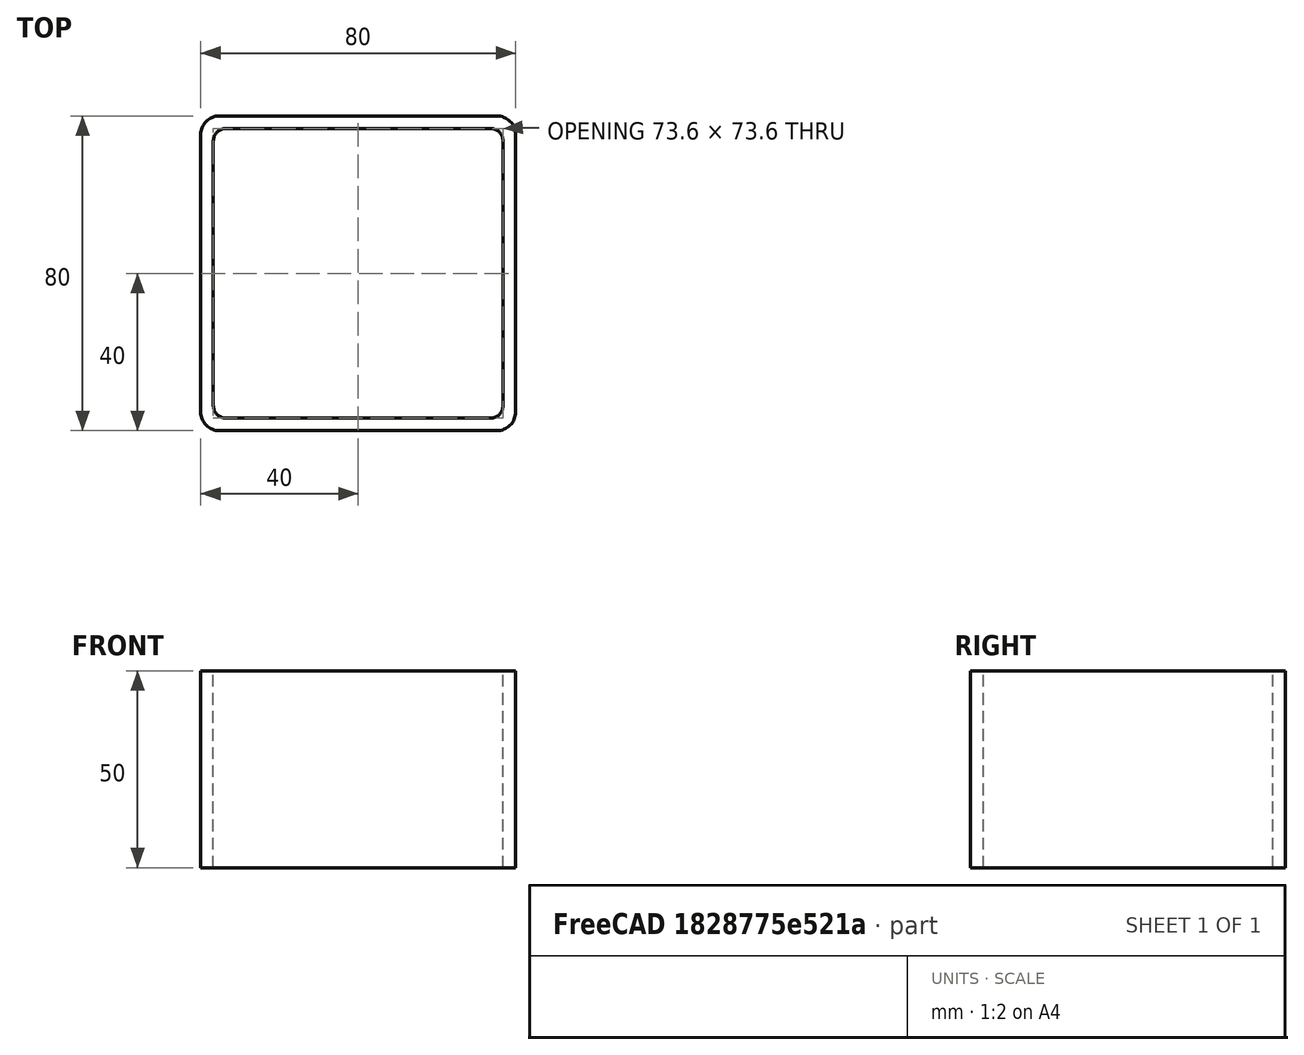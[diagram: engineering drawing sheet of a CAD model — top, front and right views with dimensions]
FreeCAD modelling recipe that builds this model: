
FCSTD DOCUMENT  (FreeCAD 0.15R4671 (Git))
Label: Square hollow section 80x80x3.2 EN10219 S235JRH
License: All rights reserved
LicenseURL: http://en.wikipedia.org/wiki/All_rights_reserved
objects: Sketcher::SketchObject×1, Part::Extrusion×1
note: 2 computed .brp shape members not serialized (recipe doc carries the construction recipe); baked Part::Feature solids carry a one-line shape summary decoded from their .brp

FEATURE [Sketcher::SketchObject] Sketch
  sketch-geometry (16):
    g0: LineSegment StartX=-33.6 StartY=36.8 StartZ=0 EndX=33.6 EndY=36.8 EndZ=0
    g1: LineSegment StartX=36.8 StartY=33.6 StartZ=0 EndX=36.8 EndY=-33.6 EndZ=0
    g2: LineSegment StartX=33.6 StartY=-36.8 StartZ=0 EndX=-33.6 EndY=-36.8 EndZ=0
    g3: LineSegment StartX=-36.8 StartY=-33.6 StartZ=0 EndX=-36.8 EndY=33.6 EndZ=0
    g4: LineSegment StartX=-35.2 StartY=40 StartZ=0 EndX=35.2 EndY=40 EndZ=0
    g5: LineSegment StartX=40 StartY=35.2 StartZ=0 EndX=40 EndY=-35.2 EndZ=0
    g6: LineSegment StartX=35.2 StartY=-40 StartZ=0 EndX=-35.2 EndY=-40 EndZ=0
    g7: LineSegment StartX=-40 StartY=-35.2 StartZ=0 EndX=-40 EndY=35.2 EndZ=0
    g8: ArcOfCircle CenterX=-33.6 CenterY=33.6 CenterZ=0 NormalX=0 NormalY=0 NormalZ=1 Radius=3.2 StartAngle=1.5708 EndAngle=3.14159
    g9: ArcOfCircle CenterX=33.6 CenterY=33.6 CenterZ=0 NormalX=0 NormalY=0 NormalZ=1 Radius=3.2 StartAngle=0 EndAngle=1.5708
    g10: ArcOfCircle CenterX=33.6 CenterY=-33.6 CenterZ=0 NormalX=0 NormalY=0 NormalZ=1 Radius=3.2 StartAngle=4.71239 EndAngle=6.28319
    g11: ArcOfCircle CenterX=-33.6 CenterY=-33.6 CenterZ=0 NormalX=0 NormalY=0 NormalZ=1 Radius=3.2 StartAngle=3.14159 EndAngle=4.71239
    g12: ArcOfCircle CenterX=35.2 CenterY=35.2 CenterZ=0 NormalX=0 NormalY=0 NormalZ=1 Radius=4.8 StartAngle=0 EndAngle=1.5708
    g13: ArcOfCircle CenterX=35.2 CenterY=-35.2 CenterZ=0 NormalX=0 NormalY=0 NormalZ=1 Radius=4.8 StartAngle=4.71239 EndAngle=6.28319
    g14: ArcOfCircle CenterX=-35.2 CenterY=-35.2 CenterZ=0 NormalX=0 NormalY=0 NormalZ=1 Radius=4.8 StartAngle=3.14159 EndAngle=4.71239
    g15: ArcOfCircle CenterX=-35.2 CenterY=35.2 CenterZ=0 NormalX=0 NormalY=0 NormalZ=1 Radius=4.8 StartAngle=1.5708 EndAngle=3.14159
  constraints (36):
    c: Horizontal(g2)
    c: Vertical(g3)
    c: Horizontal(g6)
    c: Vertical(g7)
    c: Tangent(g3,g8) = 1.5708
    c: Tangent(g0,g8) = 1.5708
    c: Tangent(g0,g9) = 1.5708
    c: Tangent(g1,g9) = 1.5708
    c: Tangent(g1,g10) = 1.5708
    c: Tangent(g2,g10) = 1.5708
    c: Tangent(g2,g11) = 1.5708
    c: Tangent(g3,g11) = 1.5708
    c: Tangent(g4,g12) = 1.5708
    c: Tangent(g5,g12) = 1.5708
    c: Tangent(g5,g13) = 1.5708
    c: Tangent(g6,g13) = 1.5708
    c: Tangent(g6,g14) = 1.5708
    c: Tangent(g7,g14) = 1.5708
    c: Tangent(g7,g15) = 1.5708
    c: Tangent(g4,g15) = 1.5708
    c: Equal(g9,g8)
    c: Equal(g9,g11)
    c: Equal(g9,g10)
    c: Equal(g12,g15)
    c: Equal(g12,g14)
    c: Equal(g12,g13)
    c: Symmetric(g4,g6,g-1)
    c: Symmetric(g7,g5,g-2)
    c: DistanceY(g4,g6) = -80
    c: DistanceX(g7,g5) = 80
    c: Symmetric(g3,g1,g-2)
    c: Symmetric(g0,g2,g-1)
    c: DistanceY(g0,g4) = 3.2
    c: DistanceX(g5,g1) = -3.2
    c: Radius(g9) = 3.2
    c: Radius(g12) = 4.8
FEATURE [Part::Extrusion] Extrude  label="Square hollow section 80x80x3.2 EN10219 S235JRH"
  Base = -> Sketch
  Dir = (0,0,50)
  Solid = true
